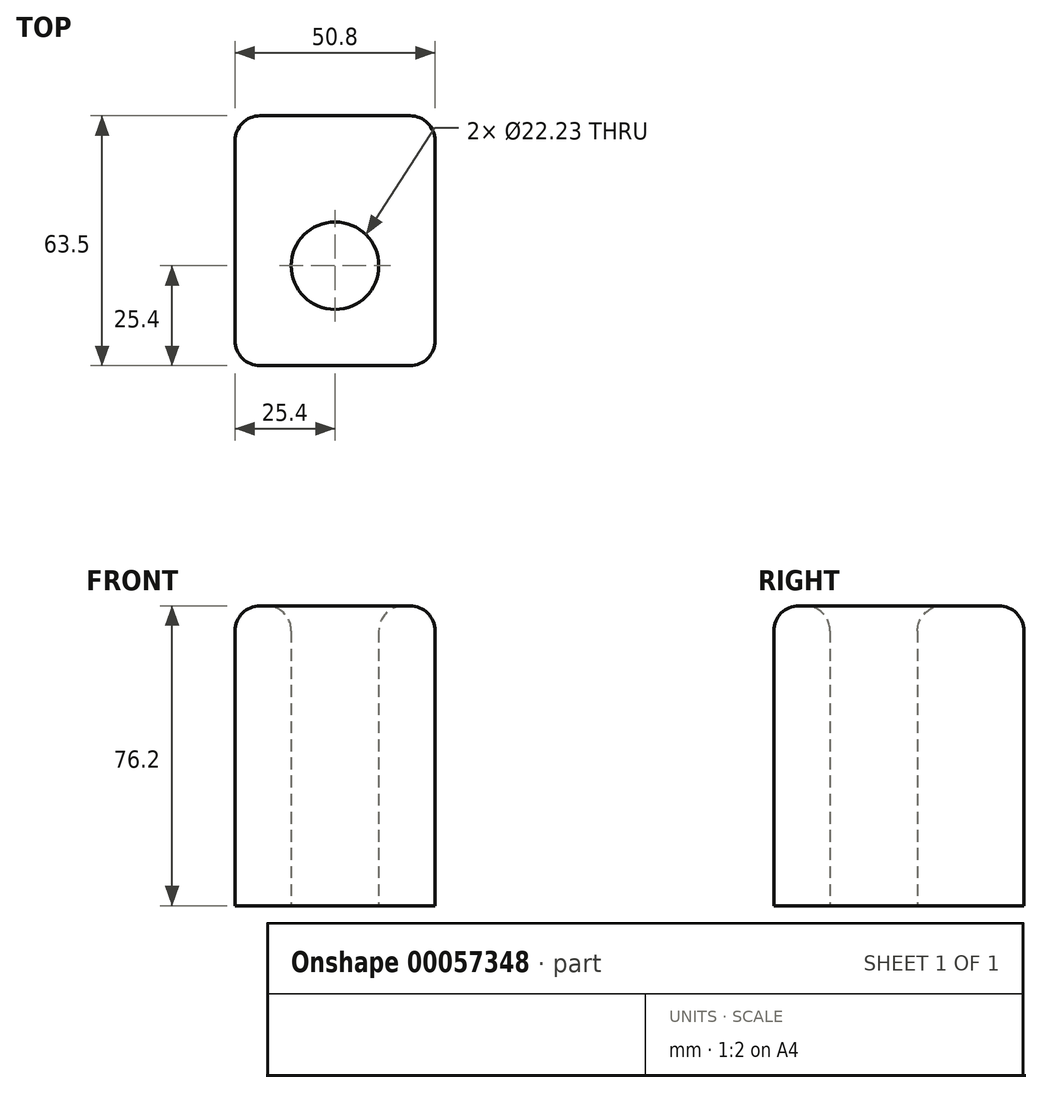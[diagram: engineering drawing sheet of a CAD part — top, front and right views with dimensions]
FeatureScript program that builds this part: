
annotation { "Feature Type Name" : "Feature", "Feature Type Description" : "" }
export const myFeature = defineFeature(function(context is Context, id is Id, definition is map)
    precondition{}
    {
        {
            var Q0;
            Q0=qCreatedBy(makeId("Top.planeOp"),FACE);
            var sketch = newSketch(context, id + "F0", { "sketchPlane" : qUnion([Q0])});
            skLineSegment(sketch, "E0.bottom", {"start": v(0, 0) * mm, "end": v(-50.8, 0) * mm});
            skLineSegment(sketch, "E0.top", {"start": v(0, 63.5) * mm, "end": v(-50.8, 63.5) * mm});
            skLineSegment(sketch, "E0.left", {"start": v(0, 0) * mm, "end": v(0, 63.5) * mm});
            skLineSegment(sketch, "E0.right", {"start": v(-50.8, 0) * mm, "end": v(-50.8, 63.5) * mm});
            skCircle(sketch, "E1", {"center": v(-25.4, 25.4) * mm, "radius": 11.11 * mm});
            skSolve(sketch);
        }
        {
            var Q0;
            Q0 = qSketchRegion(id + "F0", true);
            extrude(context, id + "F1", {"entities" : qUnion([Q0]), "endBound" : BoundingType.SYMMETRIC, "depth" : 76.2 * mm});
        }
        {
            var Q0;
            Q0=makeQuery(id+"F1.opExtrude","SWEPT_EDGE",EDGE,{"disambiguationData":[OSD([sQuery(id+"F0.wireOp",EDGE,"E0.top"),sQuery(id+"F0.wireOp",EDGE,"E0.right")])]});
            var Q1;
            Q1=makeQuery(id+"F1.opExtrude","SWEPT_EDGE",EDGE,{"disambiguationData":[OSD([sQuery(id+"F0.wireOp",EDGE,"E0.top"),sQuery(id+"F0.wireOp",EDGE,"E0.left")])]});
            var Q2;
            Q2=makeQuery(id+"F1.opExtrude","SWEPT_EDGE",EDGE,{"disambiguationData":[OSD([sQuery(id+"F0.wireOp",EDGE,"E0.bottom"),sQuery(id+"F0.wireOp",EDGE,"E0.right")])]});
            var Q3;
            Q3=makeQuery(id+"F1.opExtrude","SWEPT_EDGE",EDGE,{"disambiguationData":[OSD([sQuery(id+"F0.wireOp",EDGE,"E0.bottom"),sQuery(id+"F0.wireOp",EDGE,"E0.left")])]});
            var Q4;
            Q4=makeQuery(id+"F1.opExtrude","CAP_FACE",FACE,{"disambiguationData":[OSD([sQuery(id+"F0.wireOp",EDGE,"E0.bottom"),sQuery(id+"F0.wireOp",EDGE,"E0.top"),sQuery(id+"F0.wireOp",EDGE,"E0.left"),sQuery(id+"F0.wireOp",EDGE,"E0.right"),sQuery(id+"F0.wireOp",EDGE,"E1")])],"isStart":false});
            fillet(context, id + "F2", {"entities" : qUnion([Q0, Q1, Q2, Q3, Q4]), "radius" : 6.35 * mm, "tangentPropagation" : true, "allowEdgeOverflow" : false});
        }
    });
